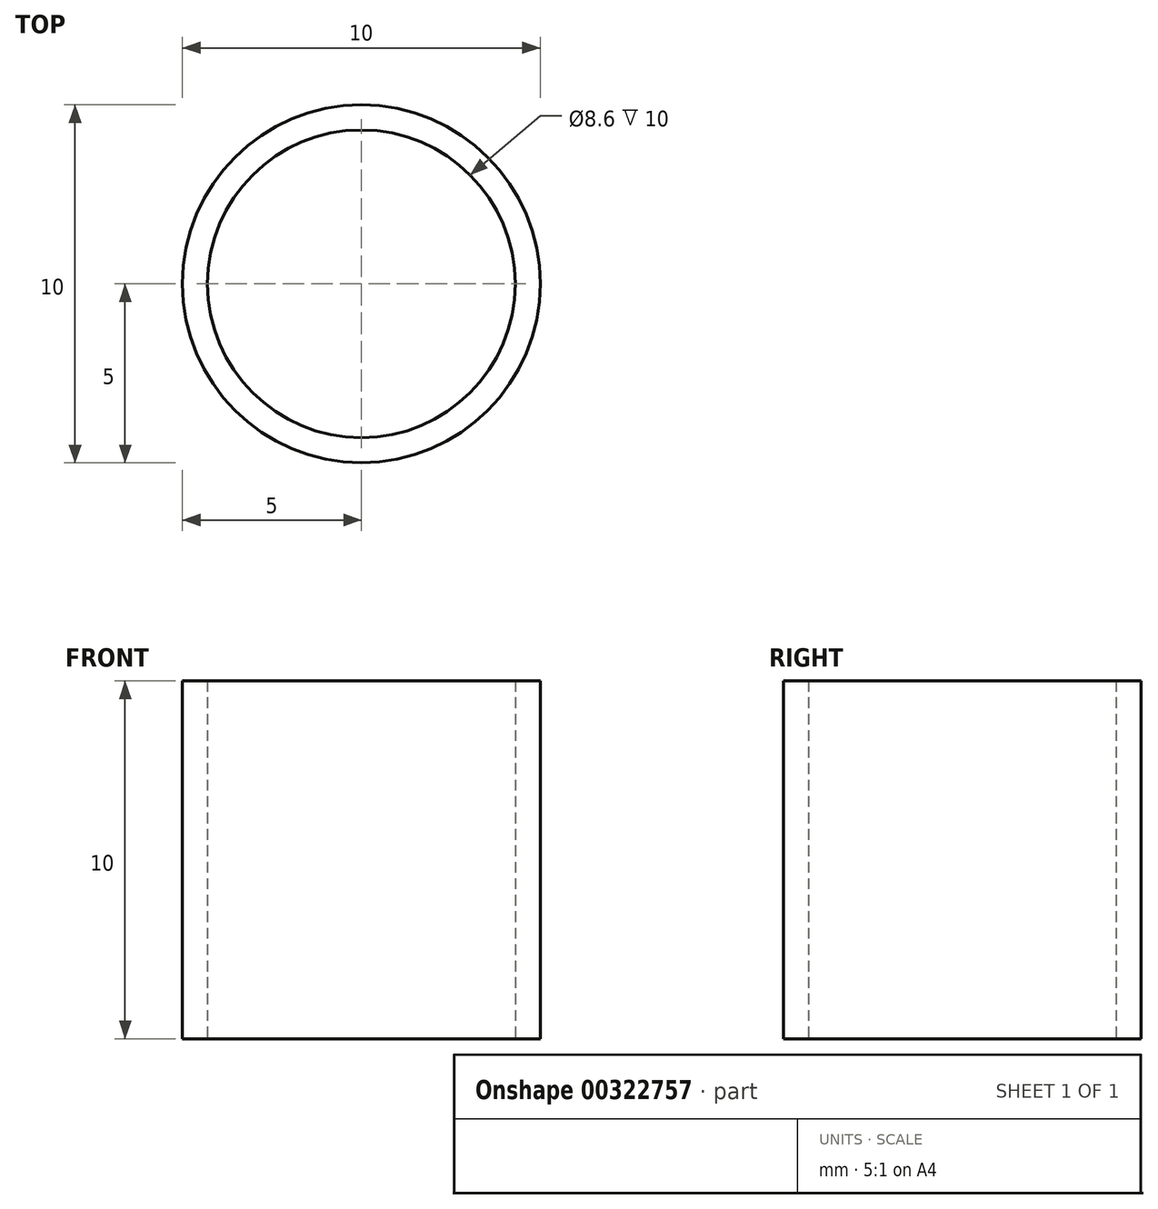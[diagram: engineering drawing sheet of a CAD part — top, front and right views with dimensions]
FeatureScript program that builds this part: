
annotation { "Feature Type Name" : "Feature", "Feature Type Description" : "" }
export const myFeature = defineFeature(function(context is Context, id is Id, definition is map)
    precondition{}
    {
        {
            var Q0;
            Q0=qCreatedBy(makeId("Top.planeOp"),FACE);
            var sketch = newSketch(context, id + "F0", { "sketchPlane" : qUnion([Q0])});
            skCircle(sketch, "E0", {"center": v(0, 0) * mm, "radius": 5 * mm});
            skCircle(sketch, "E1", {"center": v(0, 0) * mm, "radius": 4.3 * mm});
            skSolve(sketch);
        }
        {
            var Q0;
            Q0=makeQuery(id+"F0.imprint","IMPRINT",FACE,{"disambiguationData":[TD([[makeQuery(id+"F0.imprint","IMPRINT",EDGE,{"derivedFrom":sQuery(id+"F0.wireOp",EDGE,"E0")}),1.0]])]});
            extrude(context, id + "F1", {"entities" : qUnion([Q0]), "depth" : 10 * mm});
        }
    });
